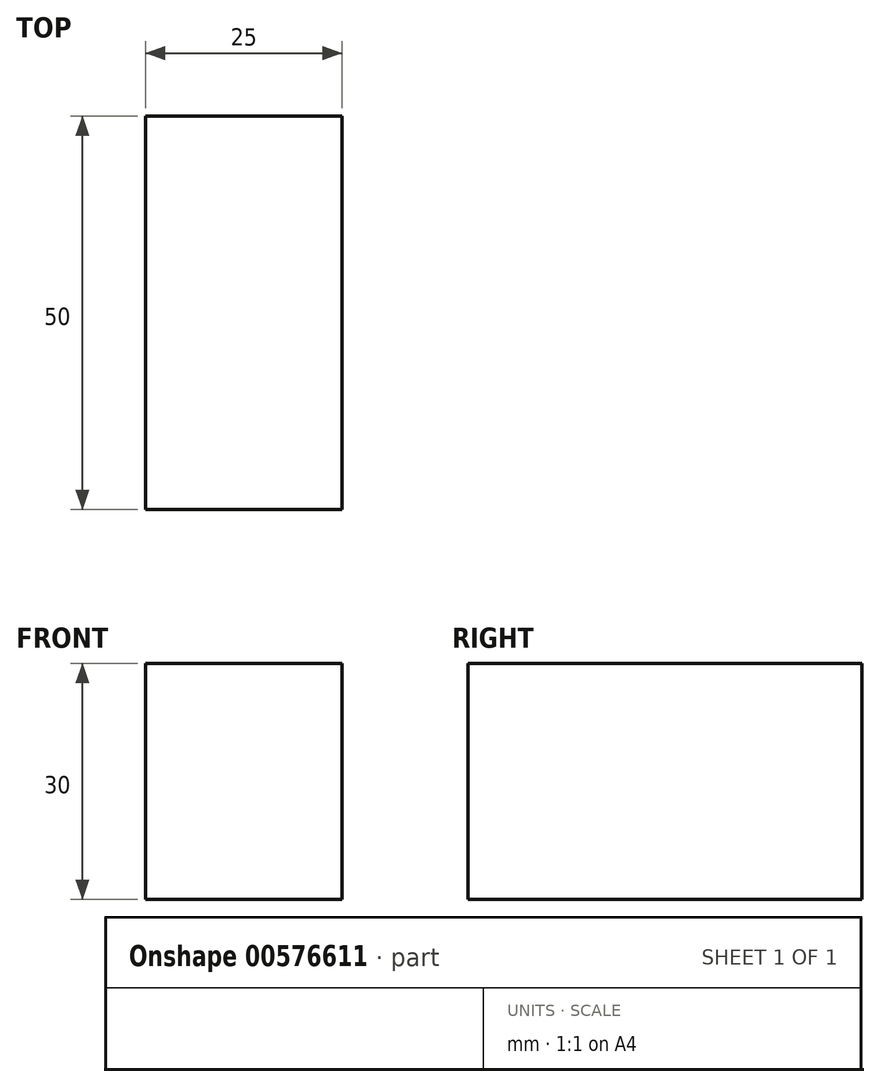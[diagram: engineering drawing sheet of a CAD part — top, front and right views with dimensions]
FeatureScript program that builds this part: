
annotation { "Feature Type Name" : "Feature", "Feature Type Description" : "" }
export const myFeature = defineFeature(function(context is Context, id is Id, definition is map)
    precondition{}
    {
        {
            var Q0;
            Q0=qCreatedBy(makeId("Top.planeOp"),FACE);
            var sketch = newSketch(context, id + "F0", { "sketchPlane" : qUnion([Q0])});
            skLineSegment(sketch, "E0.bottom", {"start": v(0, 0) * mm, "end": v(25, 0) * mm});
            skLineSegment(sketch, "E0.top", {"start": v(0, 50) * mm, "end": v(25, 50) * mm});
            skLineSegment(sketch, "E0.left", {"start": v(0, 0) * mm, "end": v(0, 50) * mm});
            skLineSegment(sketch, "E0.right", {"start": v(25, 0) * mm, "end": v(25, 50) * mm});
            skSolve(sketch);
        }
        {
            var Q0;
            Q0 = qSketchRegion(id + "F0", true);
            extrude(context, id + "F1", {"entities" : qUnion([Q0]), "depth" : 30 * mm, "offsetDistance" : 25 * mm});
        }
    });
